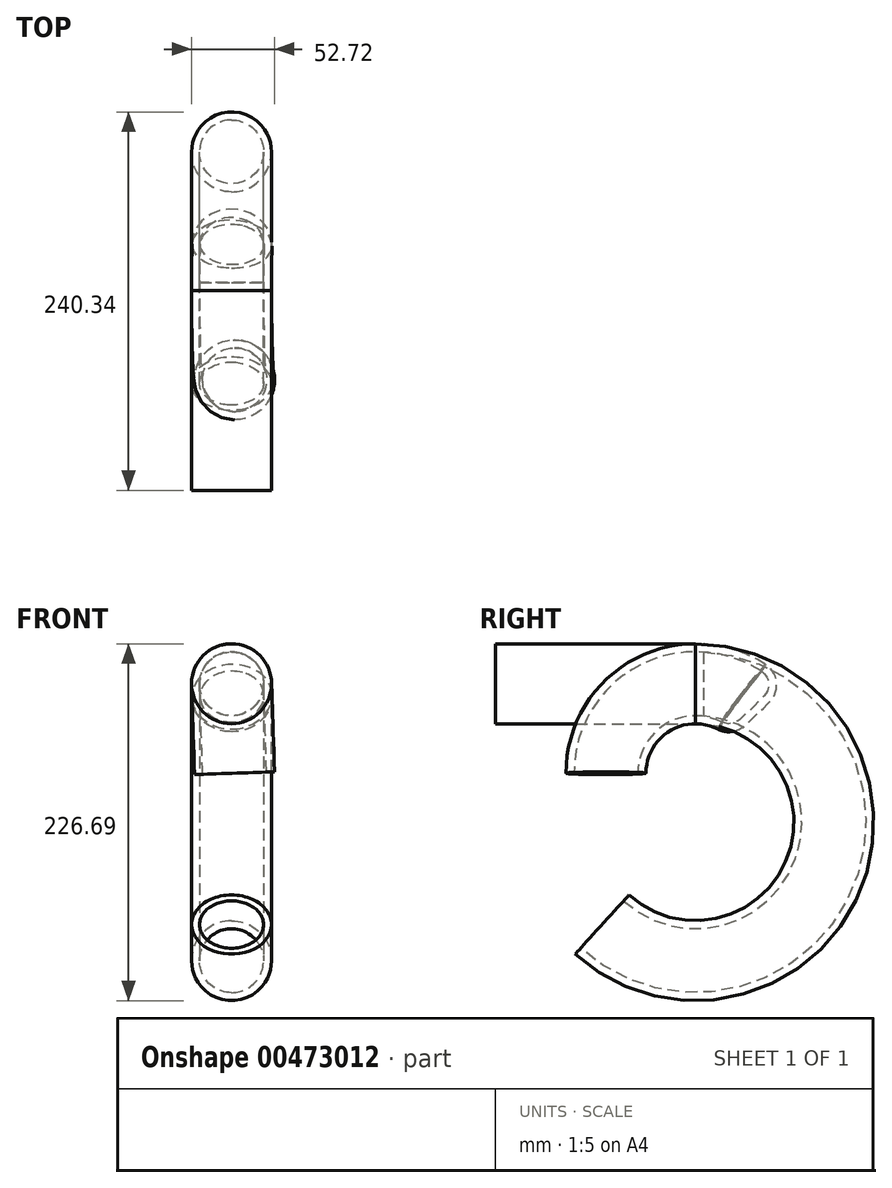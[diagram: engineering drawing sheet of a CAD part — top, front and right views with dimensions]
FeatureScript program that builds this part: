
annotation { "Feature Type Name" : "Feature", "Feature Type Description" : "" }
export const myFeature = defineFeature(function(context is Context, id is Id, definition is map)
    precondition{}
    {
        {
            var Q0;
            Q0=qCreatedBy(makeId("Front.planeOp"),FACE);
            var sketch = newSketch(context, id + "F0", { "sketchPlane" : qUnion([Q0])});
            skCircle(sketch, "E0", {"center": v(0, 0) * mm, "radius": 25.4 * mm});
            skLineSegment(sketch, "E1", {"start": v(0, -56.87) * mm, "end": v(99.85, -53.46) * mm});
            skSolve(sketch);
        }
        {
            var Q0;
            Q0=qCreatedBy(makeId("Right.planeOp"),FACE);
            var sketch = newSketch(context, id + "F1", { "sketchPlane" : qUnion([Q0])});
            skArc(sketch, "E2", {"start": v(-59.24, -152.94) * mm, "mid": v(82, -119.71) * mm, "end": v(0, 0) * mm});
            skSolve(sketch);
        }
        {
            var Q0;
            Q0=makeQuery(id+"F0.imprint","IMPRINT",FACE,{"disambiguationData":[TD([[makeQuery(id+"F0.imprint","IMPRINT",EDGE,{"derivedFrom":sQuery(id+"F0.wireOp",EDGE,"E0")}),1.0]])]});
            var Q1;
            Q1=sQuery(id+"F1.wireOp",EDGE,"E2");
            sweep(context, id + "F2", {"profiles" : qUnion([Q0]), "path" : qUnion([Q1])});
        }
        {
            var Q0;
            Q0=makeQuery(id+"F0.imprint","IMPRINT",FACE,{"disambiguationData":[TD([[makeQuery(id+"F0.imprint","IMPRINT",EDGE,{"derivedFrom":sQuery(id+"F0.wireOp",EDGE,"E0")}),1.0]])]});
            extrude(context, id + "F3", {"entities" : qUnion([Q0]), "depth" : 127 * mm});
        }
        {
            var Q0;
            Q0=makeQuery(id+"F0.imprint","IMPRINT",FACE,{"disambiguationData":[TD([[makeQuery(id+"F0.imprint","IMPRINT",EDGE,{"derivedFrom":sQuery(id+"F0.wireOp",EDGE,"E0")}),1.0]])]});
            var Q1;
            Q1=sQuery(id+"F0.wireOp",EDGE,"E0");
            var Q2;
            Q2=sQuery(id+"F0.wireOp",EDGE,"E1");
            revolve(context, id + "F4", {"entities" : qUnion([Q0]), "surfaceEntities" : qUnion([Q1]), "axis" : qUnion([Q2]), "revolveType" : RevolveType.TWO_DIRECTIONS, "oppositeDirection" : true, "angle" : 46 * degree, "angleBack" : 270 * degree});
        }
        {
            var Q0;
            Q0=makeQuery(id+"F4.opRevolve","CAP_FACE",FACE,{"disambiguationData":[OSD([sQuery(id+"F0.wireOp",EDGE,"E0")])],"isStart":false});
            fillet(context, id + "F5", {"entities" : qUnion([Q0]), "radius" : 15.24 * mm, "tangentPropagation" : true, "allowEdgeOverflow" : false});
        }
        {
            var Q0;
            Q0=makeQuery(id+"F4.opRevolve","CAP_FACE",FACE,{"disambiguationData":[OSD([sQuery(id+"F0.wireOp",EDGE,"E0")])],"isStart":true});
            var Q1;
            Q1=makeQuery(id+"F2.opSweep","CAP_FACE",FACE,{"disambiguationData":[OSD([sQuery(id+"F0.wireOp",EDGE,"E0"),sQuery(id+"F1.wireOp",VERTEX,"E2.start")])],"isStart":false});
            shell(context, id + "F6", {"entities" : qUnion([Q0, Q1]), "thickness" : 5.08 * mm});
        }
    });
